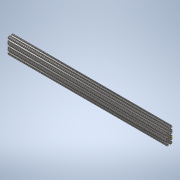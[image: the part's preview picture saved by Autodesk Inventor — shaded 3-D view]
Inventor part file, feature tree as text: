
AUTODESK INVENTOR PART (.ipt)
format: ipt  version: 2020 (Build 240168000, 168)  size: 392,192 bytes
history: native  units: in
note: dims shown in document units (in); Inventor stores cm internally (conversion verified against a paired STEP export)
features: sketch x2, extrude x1
ambient origin geometry x8: Origin, YZ Plane, XZ Plane, XY Plane, X Axis, Y Axis, Z Axis, Center Point
bodies: Solid1 (feature_tree)
feature tree (3):
  extrude  "Extrusion1"  [1 undecoded]
  sketch  "Sketch2"
  sketch  "Sketch1"  dims[d0=30.0in d1=0.0in]
note: 1 required parameter value undecoded (feature->parameter linkage not recoverable at this tier; creation-order binding heuristic only, values carry confidence <= 0.55)
